# Revit family: Soap_Dispenser-Touchless-American_Standard-777B100-Series.rfadgdgd
name_source: partatom
category: Specialty Equipment
revit_build: Autodesk Revit 2018 (Build: 20170223_1515(x64)
units: mm (PartAtom-declared; Revit-internal decimal feet)

## family parameters
Always vertical = No
Cut with Voids When Loaded = No
OmniClass Number = 23.40.20.21.34
OmniClass Title = Soap Holders, Dispensers
Part Type = Normal
Room Calculation Point = No
Round Connector Dimension = Use Diameter
Shared = Yes
Work Plane-Based = Yes

## types (2) — shared parameters
Assembly Code = C1030200
Bolt = 2 1/2"
Control Box = Yes
Control Box Pendant = Yes
Current Flow = AC Current Power
Default Elevation = 34"
Description = American Standard Touchless Sensor-Operated Foam Soap Dispenser - Battery Powered
Finish- Fasteners = Metal-American Standard
Finish- Nozzle and Tubes = Rubber-American Standard-Black
Finish- Sensor = Plastic-American Standard-Red
Height = 6 3/4"
Installation Type = Deck-Mount
Length = 6 1/2"
Manufacturer = American Standard
Mounting Nut = 1"
Mounting Nut Distance = 1"
Number of Threads = 17
Operation = Sensor Activated
Overall Height = 9 5/16"
Portion Control = Low, Medium, High & Extra High Dispense Volume Adjustment
Power Kit = Sold Separately
Price = Prices may vary. Please consult Manufacturer Representative for most up-to-date price list.
Product Documentation Link = https://www.americanstandard-us.com
Product Page URL = https://www.americanstandard-us.com
Shank = 5/16"
Shank Length = 1/8"
Soap Bottle = Yes
Soap Bottle Capacity = 1.8L
Thread = 2 1/16"
Thread Distance = 1/8"
URL = https://www.americanstandard-us.com
Warranty Information = 5-Year Limited Warranty
Waterproof Electronics = Yes
Width = 2"

## per-type parameters (varying)
| type | Finish | Material |
| 777B100.002 | Brass-American Standard-002-Polished Chrome | Brass-American Standard-002-Polished Chrome |
| 777B100.295 | Brass-American Standard-295-Brushed Nickel | Brass-American Standard-295-Brushed Nickel |

note: column(s) folded — value = type name in every type: Model

## geometry (parser evidence)
native form markers: Sweep x2
no freeform markers — native parametric forms only
